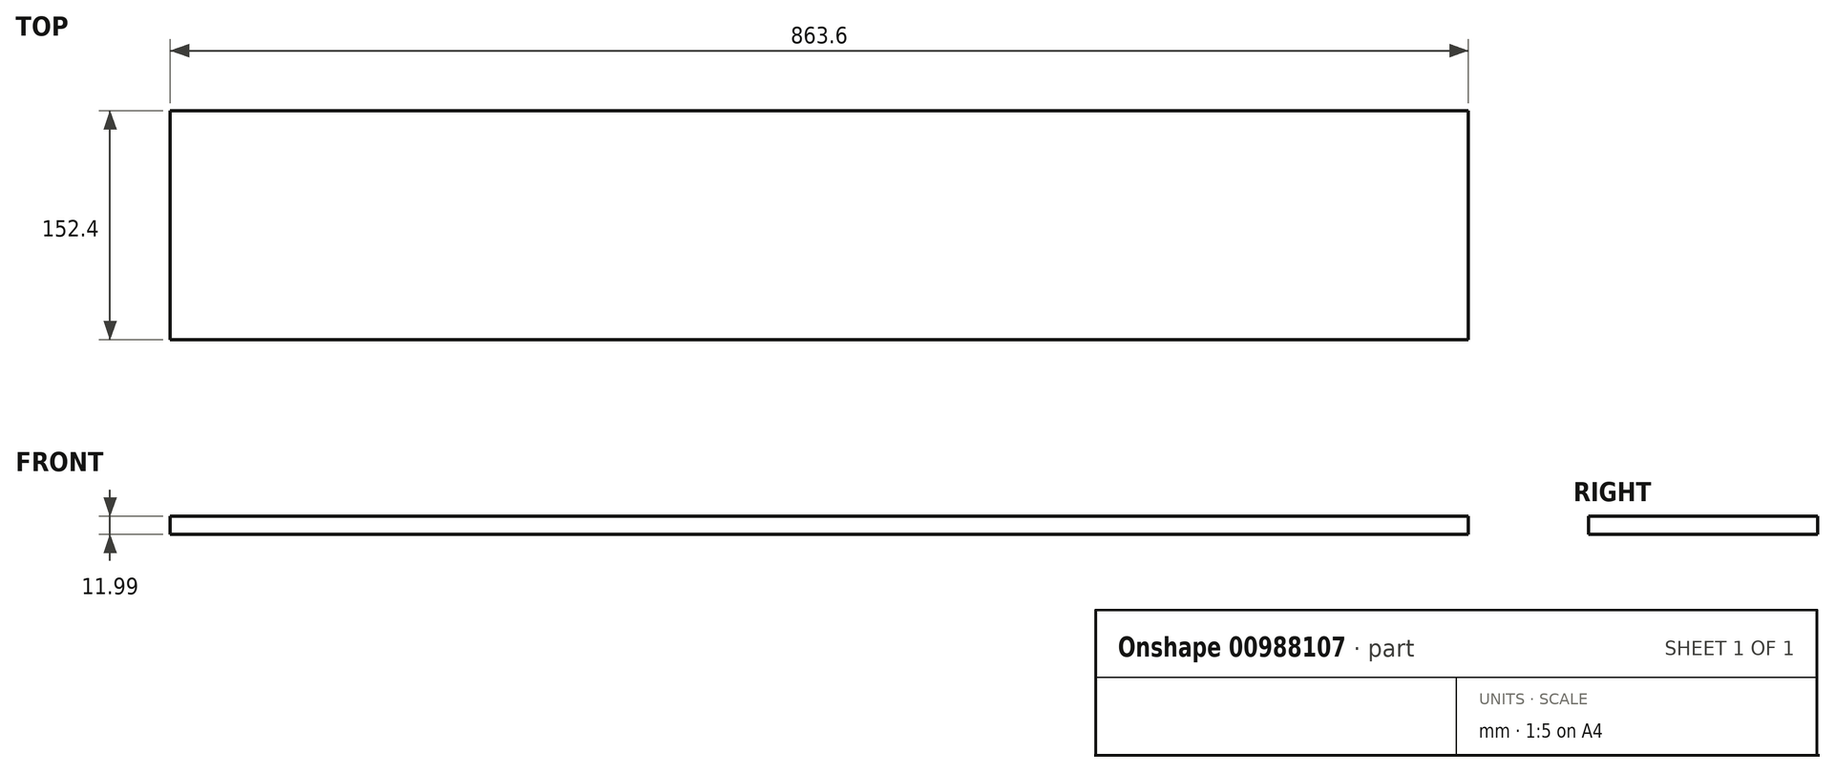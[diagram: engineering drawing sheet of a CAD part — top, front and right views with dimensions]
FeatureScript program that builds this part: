
annotation { "Feature Type Name" : "Feature", "Feature Type Description" : "" }
export const myFeature = defineFeature(function(context is Context, id is Id, definition is map)
    precondition{}
    {
        {
            var Q0;
            Q0=qCreatedBy(makeId("Top.planeOp"),FACE);
            var sketch = newSketch(context, id + "F0", { "sketchPlane" : qUnion([Q0])});
            skLineSegment(sketch, "E0.bottom", {"start": v(431.8, 76.2) * mm, "end": v(-431.8, 76.2) * mm});
            skLineSegment(sketch, "E0.top", {"start": v(431.8, -76.2) * mm, "end": v(-431.8, -76.2) * mm});
            skLineSegment(sketch, "E0.left", {"start": v(431.8, 76.2) * mm, "end": v(431.8, -76.2) * mm});
            skLineSegment(sketch, "E0.right", {"start": v(-431.8, 76.2) * mm, "end": v(-431.8, -76.2) * mm});
            skPoint(sketch, "E0.middle", {"position": v(0, 0) * mm});
            skSolve(sketch);
        }
        {
            var Q0;
            Q0=qSketchRegion(id+"F0",true);
            extrude(context, id + "F1", {"entities" : qUnion([Q0]), "depth" : 12 * mm, "offsetDistance" : 25.4 * mm});
        }
    });
